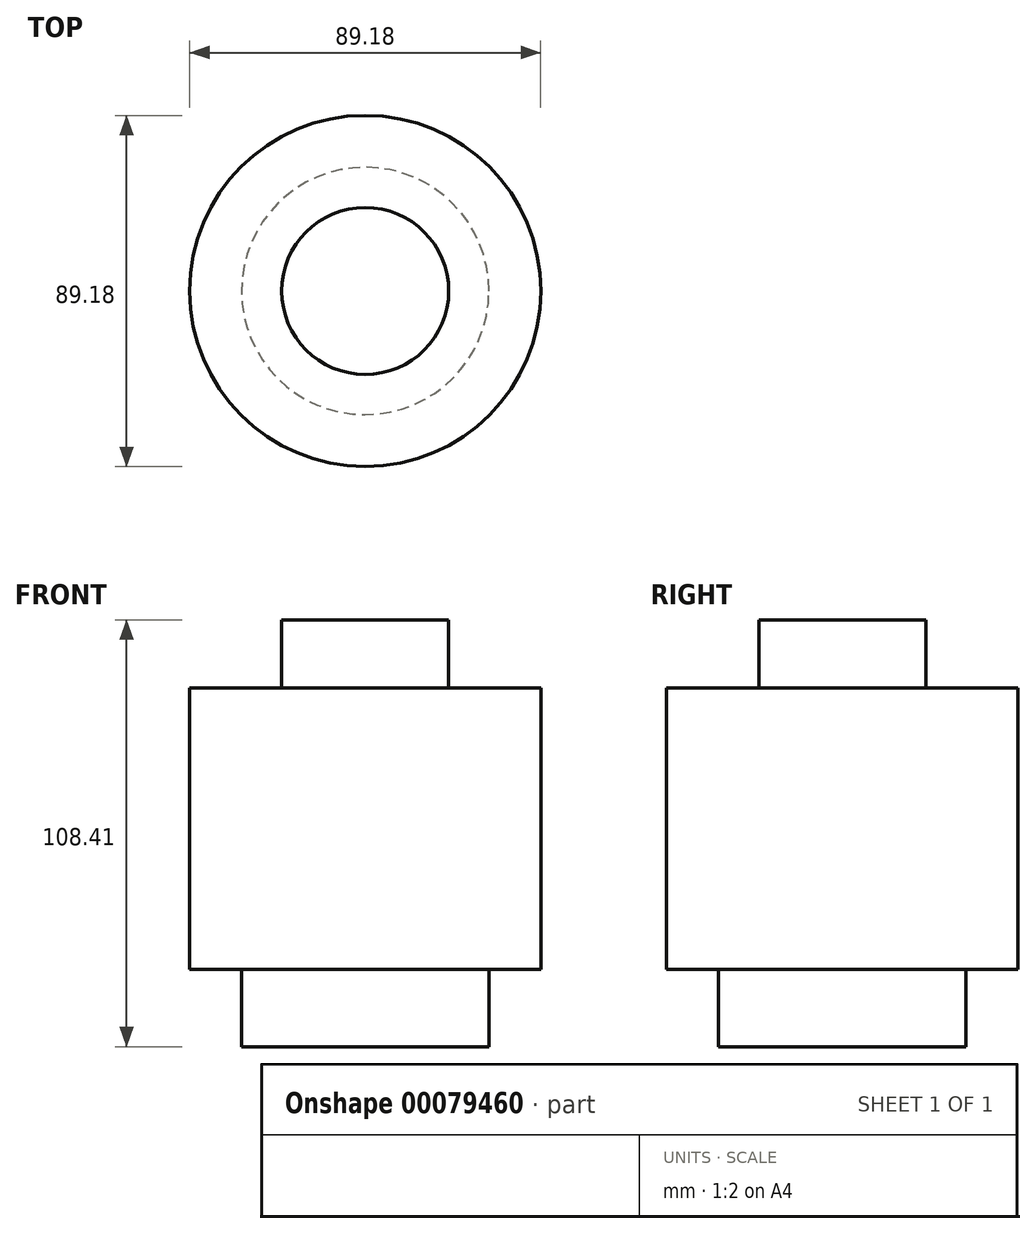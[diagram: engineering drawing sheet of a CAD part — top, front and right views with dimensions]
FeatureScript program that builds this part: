
annotation { "Feature Type Name" : "Feature", "Feature Type Description" : "" }
export const myFeature = defineFeature(function(context is Context, id is Id, definition is map)
    precondition{}
    {
        {
            var Q0;
            Q0=qCreatedBy(makeId("Top.planeOp"),FACE);
            var sketch = newSketch(context, id + "F0", { "sketchPlane" : qUnion([Q0])});
            skCircle(sketch, "E0", {"center": v(0, 0) * mm, "radius": 21.21 * mm});
            skSolve(sketch);
        }
        {
            var Q0;
            Q0=makeQuery(id+"F0.imprint","IMPRINT",FACE,{"disambiguationData":[TD([[makeQuery(id+"F0.imprint","IMPRINT",EDGE,{"derivedFrom":sQuery(id+"F0.wireOp",EDGE,"E0")}),1.0]])]});
            extrude(context, id + "F1", {"entities" : qUnion([Q0]), "depth" : 17.26 * mm});
        }
        {
            var Q0;
            Q0=qCreatedBy(makeId("Top.planeOp"),FACE);
            var sketch = newSketch(context, id + "F2", { "sketchPlane" : qUnion([Q0])});
            skCircle(sketch, "E1", {"center": v(0, 0) * mm, "radius": 44.6 * mm});
            skSolve(sketch);
        }
        {
            var Q0;
            Q0=makeQuery(id+"F2.imprint","IMPRINT",FACE,{"disambiguationData":[TD([[makeQuery(id+"F2.imprint","IMPRINT",EDGE,{"derivedFrom":sQuery(id+"F2.wireOp",EDGE,"E1")}),1.0]])]});
            extrude(context, id + "F3", {"entities" : qUnion([Q0]), "operationType" : NewBodyOperationType.ADD, "oppositeDirection" : true, "depth" : 71.54 * mm});
        }
        {
            var Q0;
            Q0=qCreatedBy(makeId("Top.planeOp"),FACE);
            var sketch = newSketch(context, id + "F4", { "sketchPlane" : qUnion([Q0])});
            skCircle(sketch, "E2", {"center": v(0, 0) * mm, "radius": 31.42 * mm});
            skSolve(sketch);
        }
        {
            var Q0;
            Q0=makeQuery(id+"F4.imprint","IMPRINT",FACE,{"disambiguationData":[TD([[makeQuery(id+"F4.imprint","IMPRINT",EDGE,{"derivedFrom":sQuery(id+"F4.wireOp",EDGE,"E2")}),1.0]])]});
            extrude(context, id + "F5", {"entities" : qUnion([Q0]), "operationType" : NewBodyOperationType.ADD, "oppositeDirection" : true, "depth" : 91.15 * mm});
        }
    });
